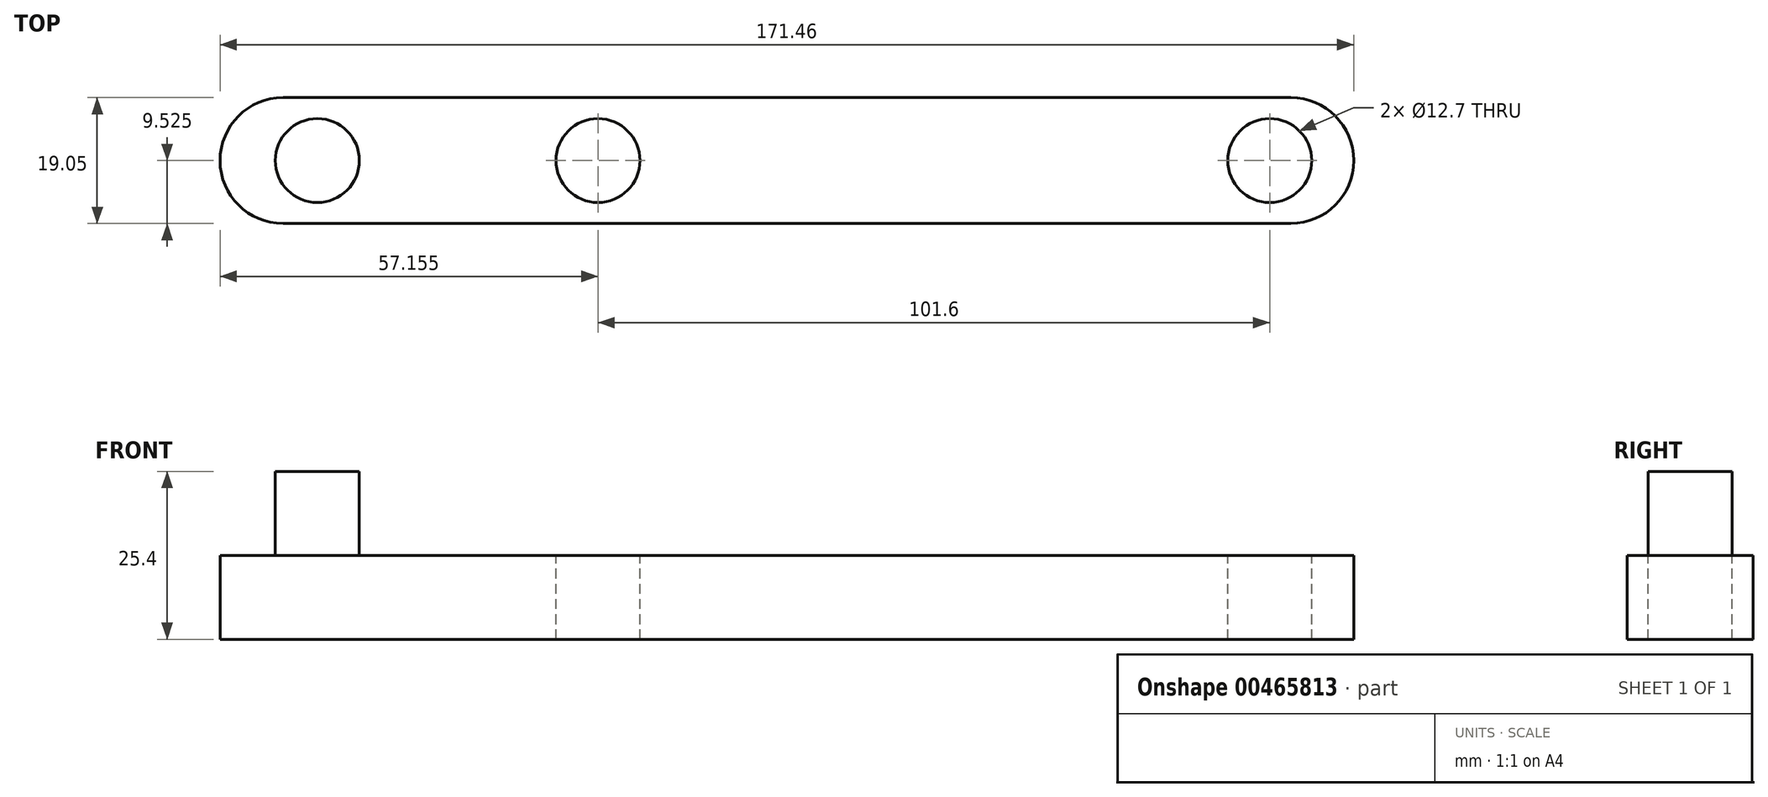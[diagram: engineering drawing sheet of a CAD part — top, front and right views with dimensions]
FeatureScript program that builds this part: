
annotation { "Feature Type Name" : "Feature", "Feature Type Description" : "" }
export const myFeature = defineFeature(function(context is Context, id is Id, definition is map)
    precondition{}
    {
        {
            var Q0;
            Q0=qCreatedBy(makeId("Top.planeOp"),FACE);
            var sketch = newSketch(context, id + "F0", { "sketchPlane" : qUnion([Q0])});
            skLineSegment(sketch, "E0", {"start": v(0, 0) * mm, "end": v(-152.4, 0) * mm});
            skLineSegment(sketch, "E1", {"start": v(-152.4, 19.05) * mm, "end": v(0, 19.05) * mm});
            skArc(sketch, "E2", {"start": v(-152.4, 19.05) * mm, "mid": v(-161.93, 9.52) * mm, "end": v(-152.4, 0) * mm});
            skPoint(sketch, "E2.third.point", {"position": v(-142.89, 10) * mm});
            skArc(sketch, "E3", {"start": v(0, 0) * mm, "mid": v(9.53, 9.53) * mm, "end": v(0, 19.05) * mm});
            skPoint(sketch, "E3.third.point", {"position": v(9.51, 9.98) * mm});
            skSolve(sketch);
        }
        {
            var Q0;
            Q0=makeQuery(id+"F0.imprint","IMPRINT",FACE,{"disambiguationData":[TD([[makeQuery(id+"F0.imprint","IMPRINT",EDGE,{"derivedFrom":sQuery(id+"F0.wireOp",EDGE,"E0")}),-1.0]])]});
            extrude(context, id + "F1", {"entities" : qUnion([Q0]), "depth" : 12.7 * mm});
        }
        {
            var Q0;
            Q0=makeQuery(id+"F1.opExtrude","CAP_FACE",FACE,{"disambiguationData":[OSD([sQuery(id+"F0.wireOp",EDGE,"E0"),sQuery(id+"F0.wireOp",EDGE,"E1"),sQuery(id+"F0.wireOp",EDGE,"E2"),sQuery(id+"F0.wireOp",EDGE,"E3")])],"isStart":false});
            var sketch = newSketch(context, id + "F2", { "sketchPlane" : qUnion([Q0])});
            skCircle(sketch, "E4", {"center": v(-104.78, 9.53) * mm, "radius": 6.35 * mm});
            skPoint(sketch, "E4.centerSnap0", {"position": v(-142.88, 9.52) * mm});
            skCircle(sketch, "E5", {"center": v(-3.17, 9.53) * mm, "radius": 6.35 * mm});
            skPoint(sketch, "E5.centerSnap0", {"position": v(9.53, 9.53) * mm});
            skSolve(sketch);
        }
        {
            var Q0;
            Q0=makeQuery(id+"F2.imprint","IMPRINT",FACE,{"disambiguationData":[TD([[makeQuery(id+"F2.imprint","IMPRINT",EDGE,{"derivedFrom":sQuery(id+"F2.wireOp",EDGE,"E4")}),1.0]])]});
            var Q1;
            Q1=makeQuery(id+"F2.imprint","IMPRINT",FACE,{"disambiguationData":[TD([[makeQuery(id+"F2.imprint","IMPRINT",EDGE,{"derivedFrom":sQuery(id+"F2.wireOp",EDGE,"E5")}),1.0]])]});
            extrude(context, id + "F3", {"entities" : qUnion([Q0, Q1]), "operationType" : NewBodyOperationType.REMOVE, "oppositeDirection" : true, "depth" : 25.4 * mm});
        }
        {
            var Q0;
            Q0=makeQuery(id+"F1.opExtrude","CAP_FACE",FACE,{"disambiguationData":[OSD([sQuery(id+"F0.wireOp",EDGE,"E0"),sQuery(id+"F0.wireOp",EDGE,"E1"),sQuery(id+"F0.wireOp",EDGE,"E2"),sQuery(id+"F0.wireOp",EDGE,"E3")])],"isStart":false});
            var sketch = newSketch(context, id + "F4", { "sketchPlane" : qUnion([Q0])});
            skCircle(sketch, "E6", {"center": v(-147.21, 9.52) * mm, "radius": 6.35 * mm});
            skPoint(sketch, "E6.centerSnap0", {"position": v(-161.93, 9.52) * mm});
            skSolve(sketch);
        }
        {
            var Q0;
            Q0=makeQuery(id+"F4.imprint","IMPRINT",FACE,{"disambiguationData":[TD([[makeQuery(id+"F4.imprint","IMPRINT",EDGE,{"derivedFrom":sQuery(id+"F4.wireOp",EDGE,"E6")}),1.0]])]});
            extrude(context, id + "F5", {"entities" : qUnion([Q0]), "operationType" : NewBodyOperationType.ADD, "depth" : 12.7 * mm});
        }
    });
